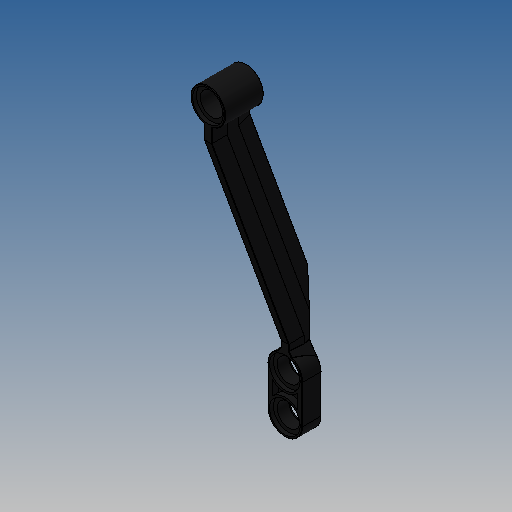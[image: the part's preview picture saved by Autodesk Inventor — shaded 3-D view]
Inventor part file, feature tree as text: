
AUTODESK INVENTOR PART (.ipt)
format: ipt  version: 2025 (Build 290162010, 162A)  size: 416,768 bytes
history: native  units: in
note: dims shown in document units (in); Inventor stores cm internally (conversion verified against a paired STEP export)
features: extrude x11, sketch x8, plane x2, sweep x1, split x1, loft x1, mirror x1, fillet x1
ambient origin geometry x8: Origin, YZ Plane, XZ Plane, XY Plane, X Axis, Y Axis, Z Axis, Center Point
bodies: Solid1 (feature_tree)
feature tree (26):
  sketch  "Sketch2"  dims[d0=0.2835in d1=0.252in]
  extrude  "Extrusion1"  Depth=0.252in
  plane  "Work Plane1"
  sketch  "Sketch3"  dims[d2=0.189in d3=0.315in]
  extrude  "Extrusion2"  Depth=0.315in
  sweep  "Sweep1"
  plane  "Work Plane2"
  split  "Split1"
  extrude  "Extrusion3"  Depth=0.2835in
  extrude  "Extrusion4"  Depth=0.189in
  extrude  "Extrusion5"  Depth=0.1575in
  extrude  "Extrusion6"  Depth=0.1102in
  extrude  "Extrusion7"  Depth=0.0039in
  extrude  "Extrusion8"  Depth=0.0039in
  extrude  "Extrusion9"  Depth=0.0039in
  sketch  "Sketch9"  dims[d13=0.0in d14=0.1102in]
  extrude  "Extrusion10"  Depth=0.0039in
  extrude  "Extrusion11"  TaperAngle=0.0deg  [1 undecoded]
  loft  "Loft1"
  mirror  "Mirror1"
  fillet  "Fillet1"  Radius=0.0315in
  sketch  "Sketch4"  dims[d4=0.0in d5=-0.315in]
  sketch  "Sketch5"  dims[d6=0.315in d7=0.2835in]
  sketch  "Sketch7"  dims[d8=0.252in d9=0.189in]
  sketch  "Sketch8"  dims[d11=2.2047in d12=0.1575in]
  sketch  "Sketch10"  dims[d15=0.1102in d16=0.0919in d17=0.063in d18=0.0945in d19=0.1102in d20=0.0in d21=0.0in d22=0.0315in d23=0.189in d24=0.063in d25=0.0in d26=0.063in d27=0.0in d28=0.0315in d29=0.0in d30=0.252in d31=0.0315in d32=0.0in d33=45.0deg d34=0.0315in d35=0.0in d36=0.0315in d37=0.0in d38=0.0472in d39=0.0in d40=0.252in d41=45.0deg d42=0.0315in d43=0.0in d44=0.0472in d45=0.0in d46=67.5deg d47=0.1109in d48=67.5deg d49=0.0in d50=90.0deg d51=0.0in d52=90.0deg d53=0.0039in d54=0.0in]
note: 1 required parameter value undecoded (feature->parameter linkage not recoverable at this tier; creation-order binding heuristic only, values carry confidence <= 0.55)
